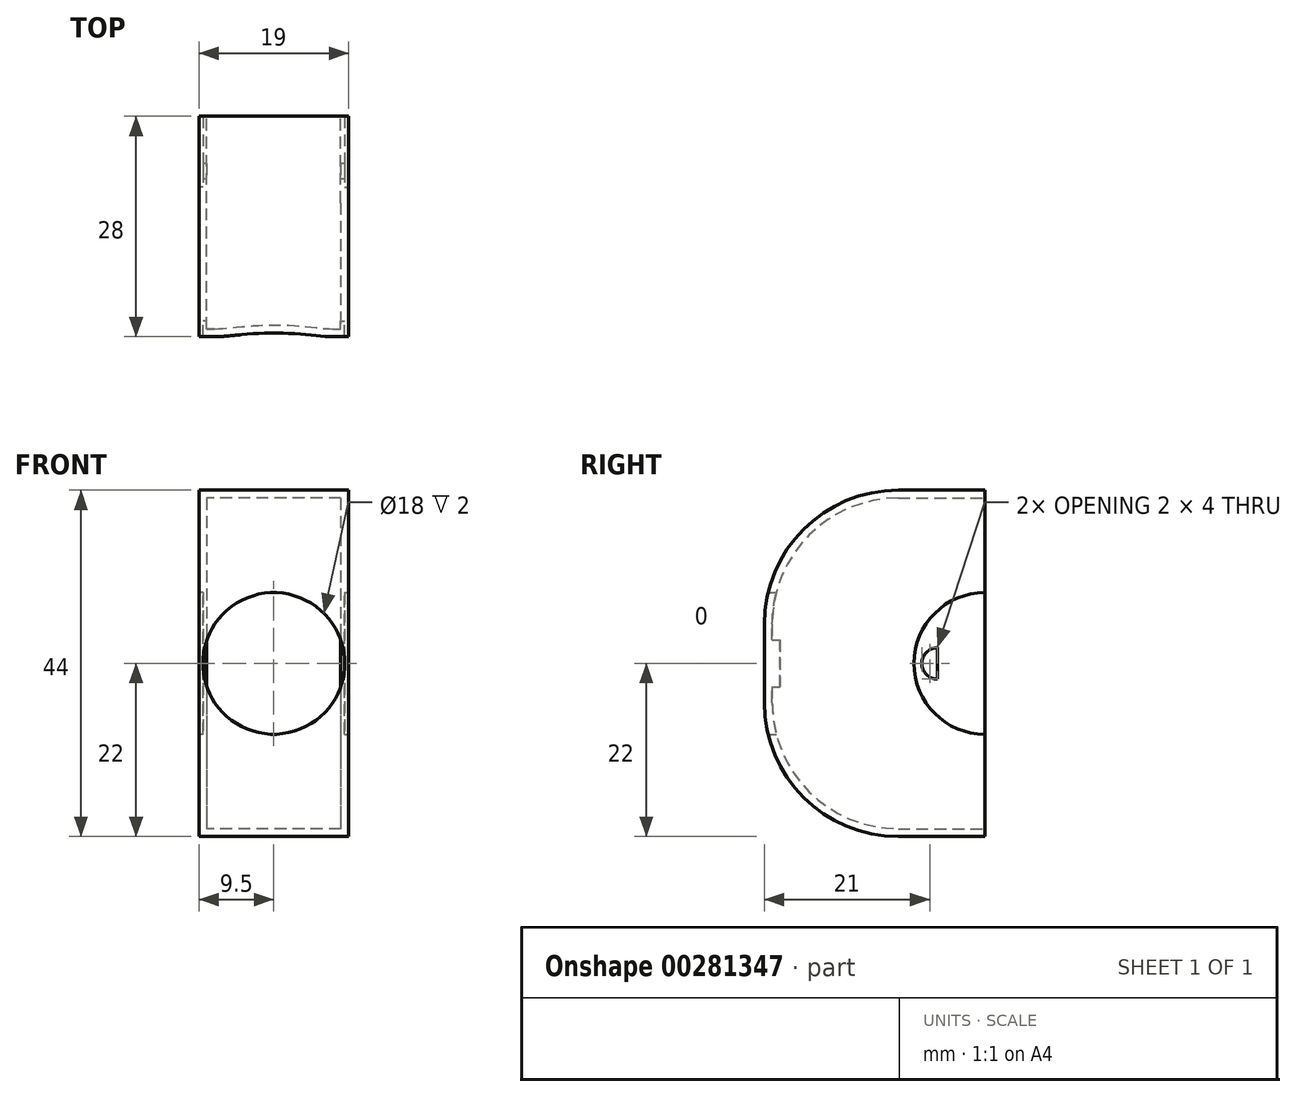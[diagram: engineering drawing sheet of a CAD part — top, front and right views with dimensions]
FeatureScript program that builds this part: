
annotation { "Feature Type Name" : "Feature", "Feature Type Description" : "" }
export const myFeature = defineFeature(function(context is Context, id is Id, definition is map)
    precondition{}
    {
        {
            var Q0;
            Q0=qCreatedBy(makeId("Front.planeOp"),FACE);
            cPlane(context, id + "F0", {"entities" : qUnion([Q0]), "cplaneType" : CPlaneType.OFFSET, "offset" : 25 * mm, "oppositeDirection" : true, "width" : 150 * mm, "height" : 150 * mm});
        }
        {
            var Q0;
            Q0=qCreatedBy(makeId("Front.planeOp"),FACE);
            var sketch = newSketch(context, id + "F1", { "sketchPlane" : qUnion([Q0])});
            skCircle(sketch, "E0", {"center": v(0, 0) * mm, "radius": 9.5 * mm});
            skSolve(sketch);
        }
        {
            var Q0;
            Q0=qCreatedBy(id+"F0.planeOp",FACE);
            var sketch = newSketch(context, id + "F2", { "sketchPlane" : qUnion([Q0])});
            skLineSegment(sketch, "E1.bottom", {"start": v(9.5, 22) * mm, "end": v(-9.5, 22) * mm});
            skLineSegment(sketch, "E1.top", {"start": v(9.5, -22) * mm, "end": v(-9.5, -22) * mm});
            skLineSegment(sketch, "E1.left", {"start": v(9.5, 22) * mm, "end": v(9.5, -22) * mm});
            skLineSegment(sketch, "E1.right", {"start": v(-9.5, 22) * mm, "end": v(-9.5, -22) * mm});
            skPoint(sketch, "E1.middle", {"position": v(0, 0) * mm});
            skSolve(sketch);
        }
        {
            var Q0;
            Q0=makeQuery(id+"F2.imprint","IMPRINT",FACE,{"disambiguationData":[TD([[makeQuery(id+"F2.imprint","IMPRINT",EDGE,{"derivedFrom":sQuery(id+"F2.wireOp",EDGE,"E1.bottom")}),1.0]])]});
            extrude(context, id + "F3", {"entities" : qUnion([Q0]), "depth" : 23 * mm});
        }
        {
            var Q0;
            Q0=makeQuery(id+"F3.opExtrude","CAP_FACE",FACE,{"disambiguationData":[OSD([sQuery(id+"F2.wireOp",EDGE,"E1.bottom"),sQuery(id+"F2.wireOp",EDGE,"E1.top"),sQuery(id+"F2.wireOp",EDGE,"E1.left"),sQuery(id+"F2.wireOp",EDGE,"E1.right")])],"isStart":true});
            extrude(context, id + "F4", {"entities" : qUnion([Q0]), "operationType" : NewBodyOperationType.ADD, "depth" : 5 * mm});
        }
        {
            var Q0;
            Q0=makeQuery(id+"F3.opExtrude","CAP_EDGE",EDGE,{"disambiguationData":[OSD([sQuery(id+"F2.wireOp",EDGE,"E1.bottom")])],"isStart":false});
            var Q1;
            Q1=makeQuery(id+"F3.opExtrude","CAP_EDGE",EDGE,{"disambiguationData":[OSD([sQuery(id+"F2.wireOp",EDGE,"E1.top")])],"isStart":false});
            fillet(context, id + "F5", {"entities" : qUnion([Q0, Q1]), "radius" : 17 * mm, "tangentPropagation" : true, "allowEdgeOverflow" : false});
        }
        {
            var Q0;
            Q0=makeQuery(id+"F4.opExtrude","CAP_FACE",FACE,{"disambiguationData":[OSD([sQuery(id+"F2.wireOp",EDGE,"E1.bottom"),sQuery(id+"F2.wireOp",EDGE,"E1.top"),sQuery(id+"F2.wireOp",EDGE,"E1.left"),sQuery(id+"F2.wireOp",EDGE,"E1.right")])],"isStart":false});
            shell(context, id + "F6", {"entities" : qUnion([Q0]), "thickness" : 1 * mm});
        }
        {
            var Q0;
            Q0=makeQuery(id+"F6.opShell","OFFSET_FACE",FACE,{"disambiguationData":[OSD([sQuery(id+"F2.wireOp",EDGE,"E1.bottom"),sQuery(id+"F2.wireOp",EDGE,"E1.top"),sQuery(id+"F2.wireOp",EDGE,"E1.left"),sQuery(id+"F2.wireOp",EDGE,"E1.right")])]});
            var sketch = newSketch(context, id + "F7", { "sketchPlane" : qUnion([Q0])});
            skCircle(sketch, "E2", {"center": v(0, 0) * mm, "radius": 9 * mm});
            skSolve(sketch);
        }
        {
            var Q0;
            Q0 = qSketchRegion(id + "F7", true);
            extrude(context, id + "F8", {"entities" : qUnion([Q0]), "operationType" : NewBodyOperationType.REMOVE, "endBound" : BoundingType.SYMMETRIC, "oppositeDirection" : true, "depth" : 2 * mm});
        }
        {
            var Q0;
            {var subQ0=sQuery(id+"F2.wireOp",EDGE,"E1.left");Q0=makeQuery(id+"F4.boolean.opBoolean","MERGE",FACE,{"derivedFrom":[makeQuery(id+"F3.opExtrude","SWEPT_FACE",FACE,{"disambiguationData":[OSD([subQ0])]}),makeQuery(id+"F4.opExtrude","SWEPT_FACE",FACE,{"disambiguationData":[OSD([subQ0])]})]});}
            var sketch = newSketch(context, id + "F9", { "sketchPlane" : qUnion([Q0])});
            skCircle(sketch, "E3", {"center": v(30, 0) * mm, "radius": 9 * mm});
            skSolve(sketch);
        }
        {
            var Q0;
            Q0 = qSketchRegion(id + "F9", true);
            extrude(context, id + "F10", {"entities" : qUnion([Q0]), "operationType" : NewBodyOperationType.REMOVE, "oppositeDirection" : true, "depth" : 0.5 * mm});
        }
        {
            var Q0;
            {var subQ0=sQuery(id+"F2.wireOp",EDGE,"E1.right");Q0=makeQuery(id+"F4.boolean.opBoolean","MERGE",FACE,{"derivedFrom":[makeQuery(id+"F3.opExtrude","SWEPT_FACE",FACE,{"disambiguationData":[OSD([subQ0])]}),makeQuery(id+"F4.opExtrude","SWEPT_FACE",FACE,{"disambiguationData":[OSD([subQ0])]})]});}
            var sketch = newSketch(context, id + "F11", { "sketchPlane" : qUnion([Q0])});
            skCircle(sketch, "E4", {"center": v(-30, 0) * mm, "radius": 9 * mm});
            skSolve(sketch);
        }
        {
            var Q0;
            Q0 = qSketchRegion(id + "F11", true);
            extrude(context, id + "F12", {"entities" : qUnion([Q0]), "operationType" : NewBodyOperationType.REMOVE, "oppositeDirection" : true, "depth" : 0.5 * mm});
        }
        {
            var Q0;
            Q0=makeQuery(id+"F12.boolean.opBoolean","COPY",FACE,{"derivedFrom":makeQuery(id+"F12.opExtrude","CAP_FACE",FACE,{"disambiguationData":[OSD([sQuery(id+"F11.wireOp",EDGE,"E4")])],"isStart":false})});
            var sketch = newSketch(context, id + "F13", { "sketchPlane" : qUnion([Q0])});
            skArc(sketch, "E5", {"start": v(-24, -2) * mm, "mid": v(-22, 0) * mm, "end": v(-24, 2) * mm});
            skPoint(sketch, "E5.centerSnap0", {"position": v(-30, 0) * mm});
            skLineSegment(sketch, "E6", {"start": v(-24, 2) * mm, "end": v(-24, -2) * mm});
            skSolve(sketch);
        }
        {
            var Q0;
            Q0=makeQuery(id+"F13.imprint","IMPRINT",FACE,{"disambiguationData":[TD([[makeQuery(id+"F13.imprint","IMPRINT",EDGE,{"derivedFrom":sQuery(id+"F13.wireOp",EDGE,"E5")}),1.0]])]});
            extrude(context, id + "F14", {"entities" : qUnion([Q0]), "operationType" : NewBodyOperationType.REMOVE, "oppositeDirection" : true, "depth" : 25 * mm});
        }
    });
